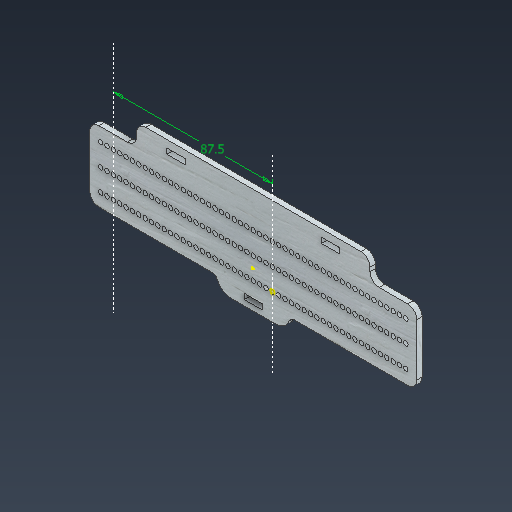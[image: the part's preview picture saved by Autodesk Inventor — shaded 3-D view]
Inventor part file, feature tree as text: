
AUTODESK INVENTOR PART (.ipt)
format: ipt  version: 2025.3 (Build 293356000, 356)  size: 442,880 bytes
history: native  units: mm
features: other x3, sketch x3, extrude x1
ambient origin geometry x8: Origin, YZ Plane, XZ Plane, XY Plane, X Axis, Y Axis, Z Axis, Center Point
bodies: Body1 (feature_tree)
feature tree (7):
  other  "實體1"
  extrude  "擠出1"  Depth=10.0mm
  sketch  "草圖3"
  sketch  "草圖5"
  sketch  "草圖1"
  other  "草圖 - 矩形陣列5"
  other  "草圖 - 矩形陣列11"
